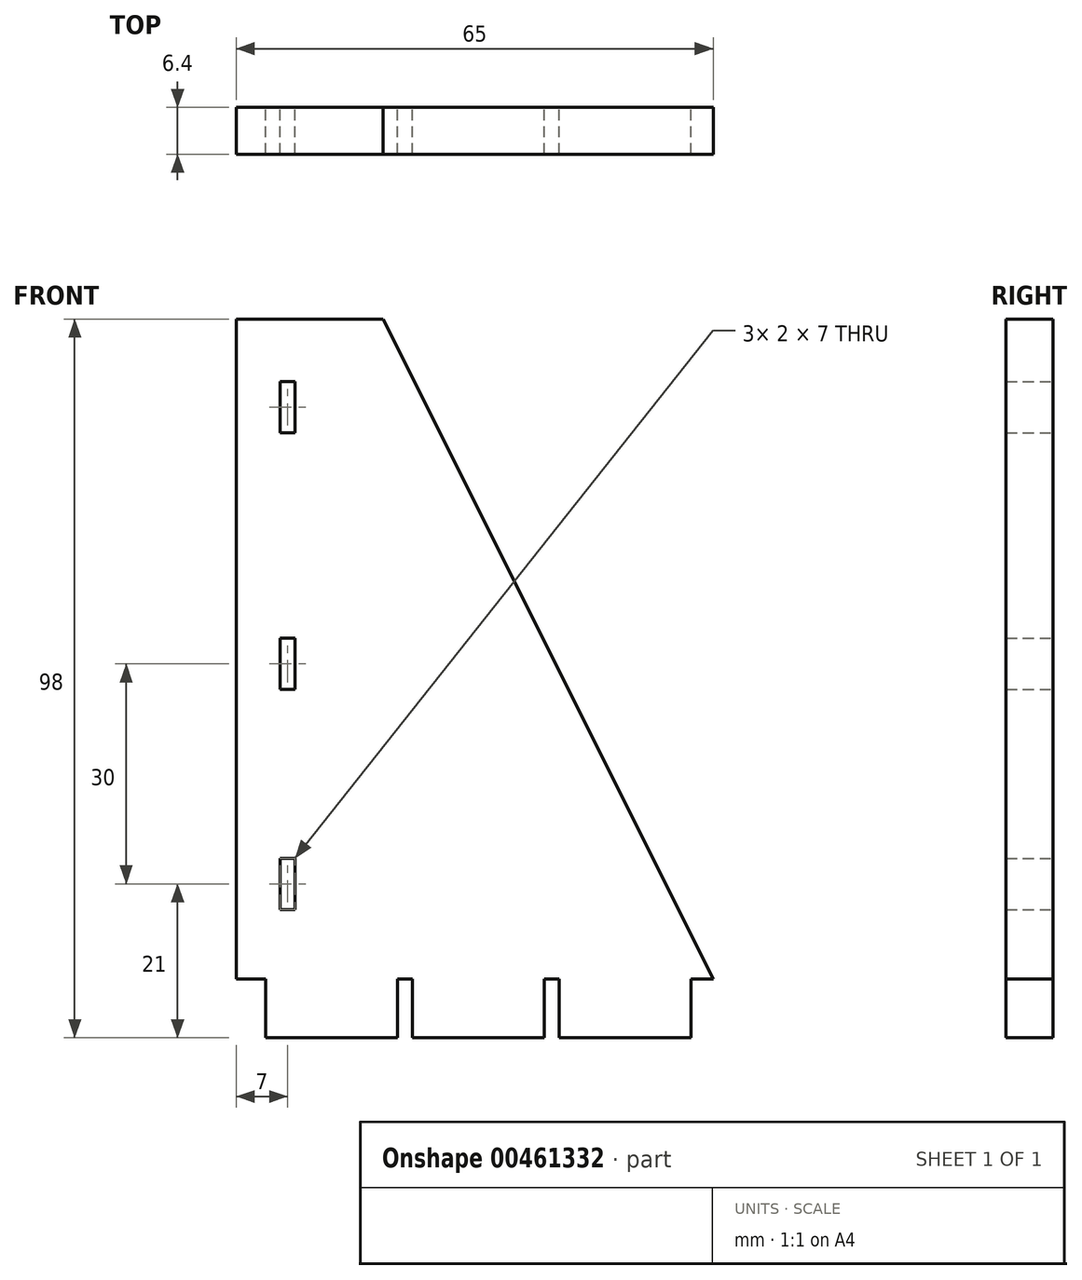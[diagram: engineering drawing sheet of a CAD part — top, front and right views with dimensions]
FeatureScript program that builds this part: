
annotation { "Feature Type Name" : "Feature", "Feature Type Description" : "" }
export const myFeature = defineFeature(function(context is Context, id is Id, definition is map)
    precondition{}
    {
        {
            var Q0;
            Q0=qCreatedBy(makeId("Front.planeOp"),FACE);
            var sketch = newSketch(context, id + "F0", { "sketchPlane" : qUnion([Q0])});
            skLineSegment(sketch, "E0", {"start": v(0, 0) * mm, "end": v(0, 90) * mm});
            skLineSegment(sketch, "E1", {"start": v(0, 90) * mm, "end": v(20, 90) * mm});
            skLineSegment(sketch, "E2", {"start": v(20, 90) * mm, "end": v(65, 0) * mm});
            skLineSegment(sketch, "E3", {"start": v(65, 0) * mm, "end": v(62, 0) * mm});
            skLineSegment(sketch, "E4.top", {"start": v(4, -8) * mm, "end": v(22, -8) * mm});
            skLineSegment(sketch, "E4.left", {"start": v(4, 0) * mm, "end": v(4, -8) * mm});
            skLineSegment(sketch, "E4.right", {"start": v(22, 0) * mm, "end": v(22, -8) * mm});
            skLineSegment(sketch, "E5.top", {"start": v(24, -8) * mm, "end": v(42, -8) * mm});
            skLineSegment(sketch, "E5.left", {"start": v(24, 0) * mm, "end": v(24, -8) * mm});
            skLineSegment(sketch, "E5.right", {"start": v(42, 0) * mm, "end": v(42, -8) * mm});
            skLineSegment(sketch, "E6.top", {"start": v(44, -8) * mm, "end": v(62, -8) * mm});
            skLineSegment(sketch, "E6.left", {"start": v(44, 0) * mm, "end": v(44, -8) * mm});
            skLineSegment(sketch, "E6.right", {"start": v(62, 0) * mm, "end": v(62, -8) * mm});
            skPoint(sketch, "E7", {"position": v(13, -8) * mm});
            skPoint(sketch, "E8", {"position": v(33, -8) * mm});
            skPoint(sketch, "E9", {"position": v(53, -8) * mm});
            skLineSegment(sketch, "E10.trimOffspring", {"start": v(44, 0) * mm, "end": v(42, 0) * mm});
            skLineSegment(sketch, "E11.trimOffspring", {"start": v(24, 0) * mm, "end": v(22, 0) * mm});
            skLineSegment(sketch, "E12.trimOffspring", {"start": v(4, 0) * mm, "end": v(0, 0) * mm});
            skLineSegment(sketch, "E13.bottom", {"start": v(8, 74.5) * mm, "end": v(6, 74.5) * mm});
            skLineSegment(sketch, "E13.top", {"start": v(8, 81.5) * mm, "end": v(6, 81.5) * mm});
            skLineSegment(sketch, "E13.left", {"start": v(8, 74.5) * mm, "end": v(8, 81.5) * mm});
            skLineSegment(sketch, "E13.right", {"start": v(6, 74.5) * mm, "end": v(6, 81.5) * mm});
            skPoint(sketch, "E13.middle", {"position": v(7, 78) * mm});
            skLineSegment(sketch, "E14", {"start": v(6, 90) * mm, "end": v(6, -4.27) * mm, "construction": true});
            skLineSegment(sketch, "E15.bottom", {"start": v(8, 39.5) * mm, "end": v(6, 39.5) * mm});
            skLineSegment(sketch, "E15.top", {"start": v(8, 46.5) * mm, "end": v(6, 46.5) * mm});
            skLineSegment(sketch, "E15.left", {"start": v(8, 39.5) * mm, "end": v(8, 46.5) * mm});
            skLineSegment(sketch, "E15.right", {"start": v(6, 39.5) * mm, "end": v(6, 46.5) * mm});
            skPoint(sketch, "E15.middle", {"position": v(7, 43) * mm});
            skLineSegment(sketch, "E16.bottom", {"start": v(8, 9.5) * mm, "end": v(6, 9.5) * mm});
            skLineSegment(sketch, "E16.top", {"start": v(8, 16.5) * mm, "end": v(6, 16.5) * mm});
            skLineSegment(sketch, "E16.left", {"start": v(8, 9.5) * mm, "end": v(8, 16.5) * mm});
            skLineSegment(sketch, "E16.right", {"start": v(6, 9.5) * mm, "end": v(6, 16.5) * mm});
            skPoint(sketch, "E16.middle", {"position": v(7, 13) * mm});
            skSolve(sketch);
        }
        {
            var Q0;
            Q0=makeQuery(id+"F0.imprint","IMPRINT",FACE,{"disambiguationData":[TD([[makeQuery(id+"F0.imprint","IMPRINT",EDGE,{"derivedFrom":sQuery(id+"F0.wireOp",EDGE,"E0")}),-1.0]])]});
            extrude(context, id + "F1", {"entities" : qUnion([Q0]), "depth" : 6.4 * mm});
        }
    });
